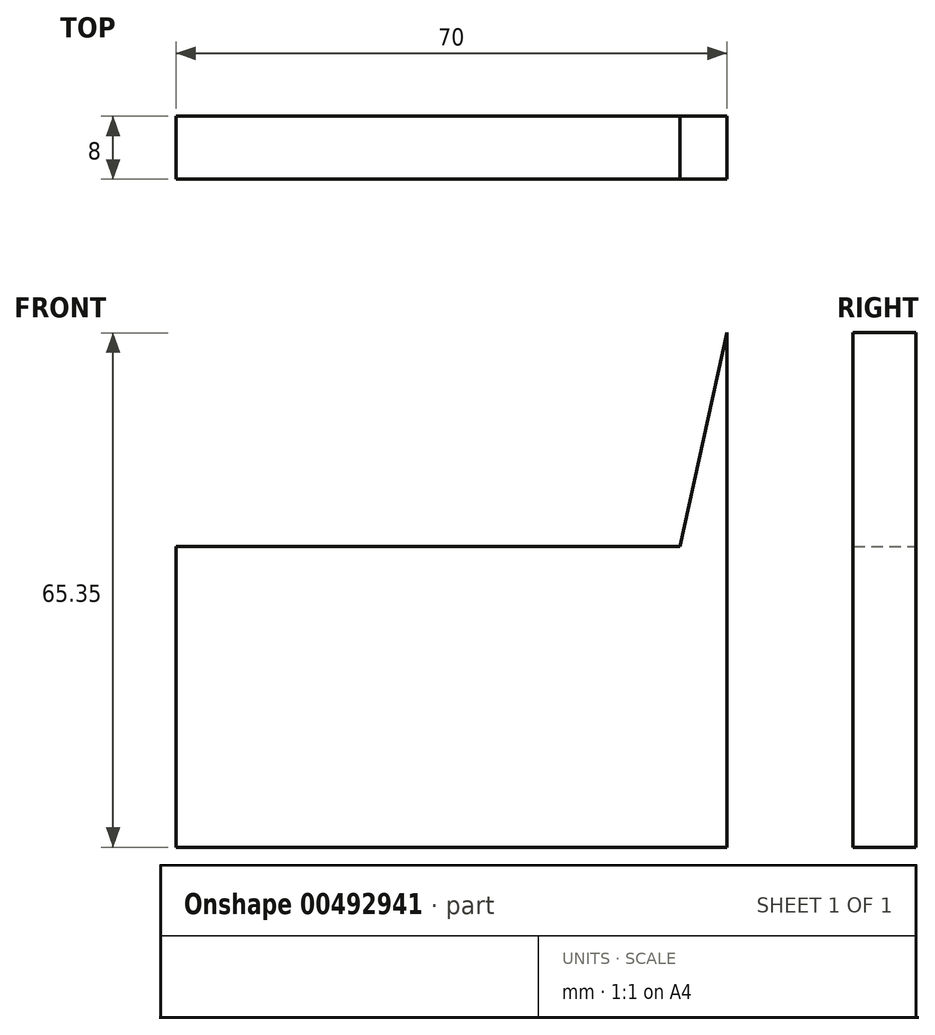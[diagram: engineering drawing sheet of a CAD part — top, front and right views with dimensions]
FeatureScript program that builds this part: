
annotation { "Feature Type Name" : "Feature", "Feature Type Description" : "" }
export const myFeature = defineFeature(function(context is Context, id is Id, definition is map)
    precondition{}
    {
        {
            var Q0;
            Q0=qCreatedBy(makeId("Front.planeOp"),FACE);
            var sketch = newSketch(context, id + "F0", { "sketchPlane" : qUnion([Q0])});
            skLineSegment(sketch, "E0.bottom", {"start": v(35, 0) * mm, "end": v(-35, 0) * mm});
            skLineSegment(sketch, "E0.left", {"start": v(35, 0) * mm, "end": v(35, 38.18) * mm});
            skLineSegment(sketch, "E0.right", {"start": v(-35, 0) * mm, "end": v(-35, 38.18) * mm});
            skLineSegment(sketch, "E1", {"start": v(35, 38.18) * mm, "end": v(35, 65.35) * mm});
            skLineSegment(sketch, "E2", {"start": v(35, 65.35) * mm, "end": v(28.98, 38.18) * mm});
            skLineSegment(sketch, "E3", {"start": v(28.98, 38.18) * mm, "end": v(-35, 38.18) * mm});
            skSolve(sketch);
        }
        {
            var Q0;
            Q0=makeQuery(id+"F0.imprint","IMPRINT",FACE,{"disambiguationData":[TD([[makeQuery(id+"F0.imprint","IMPRINT",EDGE,{"derivedFrom":sQuery(id+"F0.wireOp",EDGE,"E0.bottom")}),-1.0]])]});
            extrude(context, id + "F1", {"entities" : qUnion([Q0]), "depth" : 8 * mm});
        }
    });
